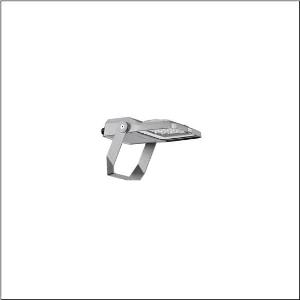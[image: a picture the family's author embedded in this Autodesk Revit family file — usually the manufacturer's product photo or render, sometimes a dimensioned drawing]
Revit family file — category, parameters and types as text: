
# Revit family: floodlight_fl_21_iq_micro___rs12_5xa7762a2b1a_2903
name_source: partatom
category: Lighting Fixtures
units: mm (PartAtom-declared; Revit-internal decimal feet)

## family parameters
Cut with Voids When Loaded = No
Host = Face
Light Source = No
Part Type = Normal
Room Calculation Point = No
Round Connector Dimension = Use Diameter
Shared = No

## types (1)
- --- (1 x LED, 3090 lm, 23.1 W, 3000K)
    Apparent Load = 23 VA
    CIE Flux Codes = 79 92 99 100 100
    Color Rendering = 70
    Color Temperature = 3000K
    Default Elevation = 1800 mm
    Description = Floodlight FL 21 iQ micro, floodlight, primary light control with lens, of PMMA, primary optical cover: protective disc, of toughened safety glass, transparent, light distribution: RS12, light emission: direct distribution, installation type: surface-mounted, LED, High Power LED, rated luminous flux: 3.090lm, luminous efficacy: 134lm/W, light colour: 730, colour temperature: 3000K, control: Auto-Match, Temp-Guard, Night-Set, Smart-Wire, Desk-Remote (wireless, voltage-free reading and setting of iQ features in the workshop via application-optimized NFC function/RFID function), optimised constant luminous flux control (CLO 2.0), Street-Remote, with terminal, 6-pole, mains connection: 220..240V, AC, 50/60Hz, start of lifetime: 23W, end of service life: 24W, reduction: 11W, luminaire housing, of diecast aluminium, powder-coated, Siteco® metallic grey (DB 702S), corrosivity category C5 mid according to DIN EN ISO 12944, sealing non-destructively replaceable, mounting bracket, of steel, galvanised, powder-coated, Siteco® metallic grey (DB 702S), protection rating (complete): IP66, insulation class (complete): insulation class II (safety insulation), certification: CE, ENEC, VDE, protection symbol: D, impact resistance: IK07, permissible operating ambient temperature: -40..+40°C, permissible operating ambient temperature for outdoor applications: -40..+50°C, standard: DIN EN 12944, LABS conformity tested according to VDMA 24364:2018-05, packaging unit: 1 piece

Light Distribution: RS12
    Height = 65 mm
    Lamp = 1 x LED
    Lamp Light Flux = 3090 lm
    Lamp Power = 23.1 W
    Lamp count = 1
    Length = 312 mm
    Luminous efficacy = 134 lm/W
    Manufacturer = Siteco
    ModVariant = No
    Model = 5XA7762A2B1A
    Number of Poles = 1
    OnlyDefault = Yes
    Power Factor = 1
    Product Name = Floodlight FL 21 iQ micro | RS12
    Product group = floodlight | pylon annexe
    ProductGroupID = 6200
    Protection Class = Protection class II
    Protection Degree = IP 66
    RLX_Detail_Level = 1
    RLX_Emergency_Light_Flux = 0 lm
    RLX_Emergency_Type = 0
    RLX_Emergency_Type_DB = No
    RlxData = <blob elided: 74813 chars, md5=e81efa70>
    Socket = socket
    Standby Power = 0 W
    System Light Flux = 3090 lm
    System Power = 23 W
    Type Comments = factory setting: luminous flux: 100 % | dim-lin: 254 | 455 mA
    Type Image = l_1006880.jpg
    URL = http://relux.com
    VarID = @adj_133269
    Voltage = 0 V
    Weight = 0.00 kg
    Width = 230 mm

## geometry (parser evidence)
native form markers: Blend x4, Sweep x12
no freeform markers — native parametric forms only
